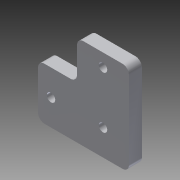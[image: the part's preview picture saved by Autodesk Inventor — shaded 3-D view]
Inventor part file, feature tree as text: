
AUTODESK INVENTOR PART (.ipt)
format: ipt  version: 2014 (Build 180170000, 170)  size: 97,792 bytes
history: native  units: in
note: dims shown in document units (in); Inventor stores cm internally (conversion verified against a paired STEP export)
features: extrude x1, fillet x1, sketch x1
ambient origin geometry x8: Origin, YZ Plane, XZ Plane, XY Plane, X Axis, Y Axis, Z Axis, Center Point
bodies: Solid1 (feature_tree)
feature tree (3):
  extrude  "Extrusion1"  Depth=1.0in
  fillet  "Fillet1"  Radius=0.163in
  sketch  "Sketch1"  dims[d0=1.75in d1=1.0in d2=0.163in d3=0.5in d4=0.25in d5=0.7874in d7=1.0in d8=0.3937in d10=1.0in d12=0.7874in d14=1.0in d15=0.3937in d17=1.0in d19=0.25in d20=0.0in d21=0.125in]
